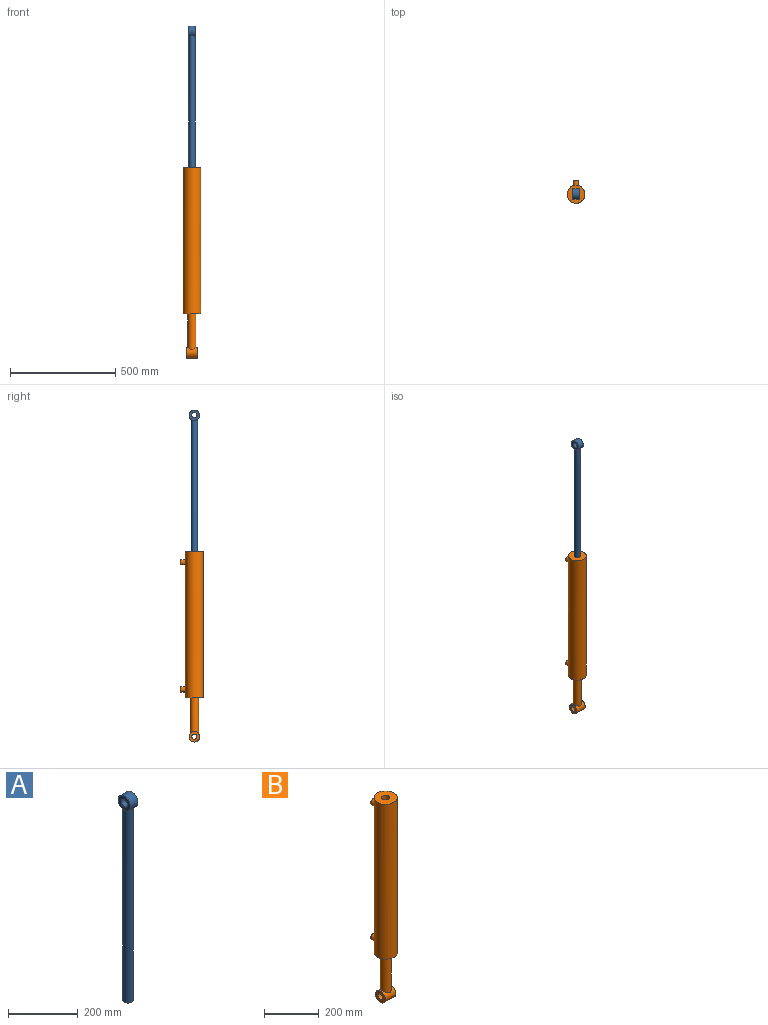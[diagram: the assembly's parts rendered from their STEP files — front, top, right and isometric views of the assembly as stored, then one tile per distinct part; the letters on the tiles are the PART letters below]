
ASSEMBLY  parts=2 mates=1
PART A: 6 faces, bbox 30x50x725 mm
  f0: cylinder r=15mm len=680mm, axis (0,0,-1), area 63846.3mm2, adj f1,f2
  f1: plane 30x30mm, normal (0,0,-1), area 706.9mm2, adj f0
  f2: cylinder r=25mm len=50mm, axis (-1,0,0), area 3968.5mm2, adj f0,f3,f4
  f3: plane 50x50mm, normal (1,0,0), area 1462.8mm2, adj f2,f5
  f4: plane 50x50mm, normal (-1,0,0), area 1462.8mm2, adj f2,f5
  f5: cylinder r=12.62mm len=30mm, axis (1,0,0), area 2379.8mm2, adj f3,f4
PART B: 14 faces, bbox 85x107.5x905 mm
  f0: cylinder r=20mm len=170mm, axis (0,0,-1), area 20695.2mm2, adj f3,f10
  f1: cylinder r=42.5mm len=695mm, axis (0,0,-1), area 184597.3mm2, adj f2,f3,f4,f6
  f2: plane 85x85mm, normal (0,0,1), area 4967.6mm2, adj f1,f12
  f3: plane 85x85mm, normal (0,0,-1), area 4417.9mm2, adj f0,f1
  f4: cylinder r=12.5mm len=25mm, axis (0,-1,0), area 1840.5mm2, adj f1,f5
  f5: plane 25x25mm, normal (0,1,0), area 490.9mm2, adj f4
  f6: cylinder r=12.5mm len=25mm, axis (0,-1,0), area 1840.5mm2, adj f1,f7
  f7: plane 25x25mm, normal (0,1,0), area 490.9mm2, adj f6
  f8: plane 50x50mm, normal (1,0,0), area 1472.6mm2, adj f10,f11
  f9: plane 50x50mm, normal (-1,0,0), area 1472.6mm2, adj f10,f11
  f10: cylinder r=25mm len=55mm, axis (-1,0,0), area 7242.6mm2, adj f0,f8,f9
  f11: cylinder r=12.5mm len=55mm, axis (-1,0,0), area 4319.7mm2, adj f8,f9
  f12: cylinder r=15mm len=50mm, axis (0,0,1), area 4712.4mm2, adj f2,f13
  f13: plane 30x30mm, normal (0,0,1), area 706.9mm2, adj f12
PLACE A t=(472.96,610.81,1286.68)mm
PLACE B t=(472.96,610.81,456.68)mm
MATE slider A.f0 <-> B.f0  axis (0,0,-1) through (472.96,610.81,1286.68)mm
